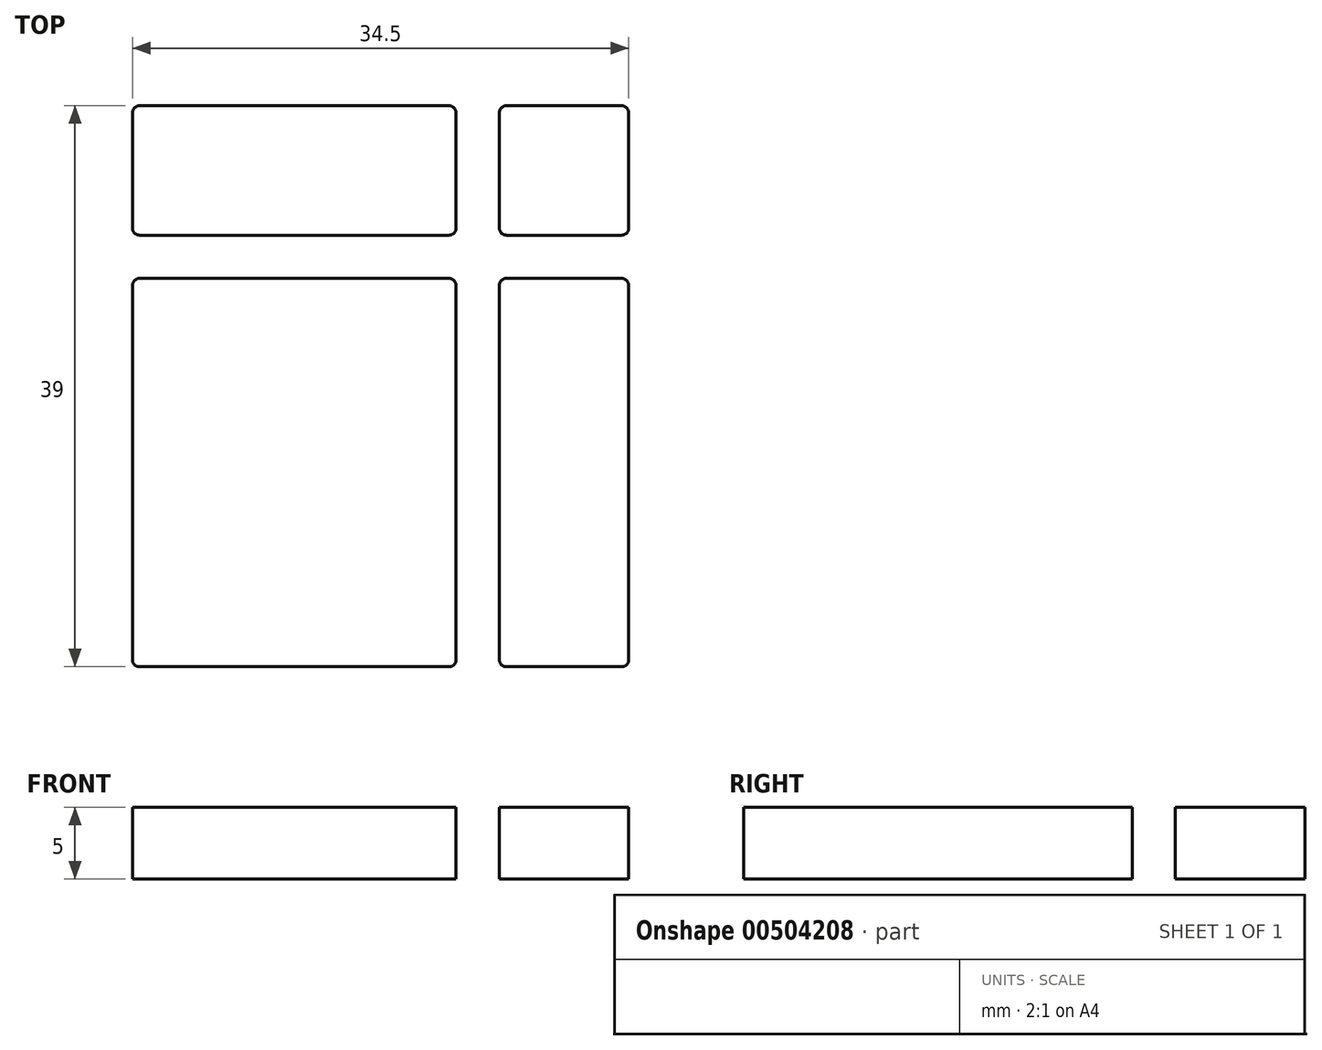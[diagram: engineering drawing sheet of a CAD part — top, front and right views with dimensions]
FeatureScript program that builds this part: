
annotation { "Feature Type Name" : "Feature", "Feature Type Description" : "" }
export const myFeature = defineFeature(function(context is Context, id is Id, definition is map)
    precondition{}
    {
        {
            var Q0;
            Q0=qCreatedBy(makeId("Top.planeOp"),FACE);
            var sketch = newSketch(context, id + "F0", { "sketchPlane" : qUnion([Q0])});
            skLineSegment(sketch, "E0.bottom", {"start": v(0.5, 0) * mm, "end": v(22, 0) * mm});
            skLineSegment(sketch, "E0.top", {"start": v(0.5, 27) * mm, "end": v(22, 27) * mm});
            skLineSegment(sketch, "E0.left", {"start": v(0, 0.5) * mm, "end": v(0, 26.5) * mm});
            skLineSegment(sketch, "E0.right", {"start": v(22.5, 0.5) * mm, "end": v(22.5, 26.5) * mm});
            skLineSegment(sketch, "E1.bottom", {"start": v(26, 0) * mm, "end": v(34, 0) * mm});
            skLineSegment(sketch, "E1.top", {"start": v(26, 27) * mm, "end": v(34, 27) * mm});
            skLineSegment(sketch, "E1.left", {"start": v(25.5, 0.5) * mm, "end": v(25.5, 26.5) * mm});
            skLineSegment(sketch, "E1.right", {"start": v(34.5, 0.5) * mm, "end": v(34.5, 26.5) * mm});
            skLineSegment(sketch, "E2.bottom", {"start": v(0.5, 30) * mm, "end": v(22, 30) * mm});
            skLineSegment(sketch, "E2.top", {"start": v(0.5, 39) * mm, "end": v(22, 39) * mm});
            skLineSegment(sketch, "E2.left", {"start": v(0, 30.5) * mm, "end": v(0, 38.5) * mm});
            skLineSegment(sketch, "E2.right", {"start": v(22.5, 30.5) * mm, "end": v(22.5, 38.5) * mm});
            skLineSegment(sketch, "E3.bottom", {"start": v(26, 30) * mm, "end": v(34, 30) * mm});
            skLineSegment(sketch, "E3.top", {"start": v(26, 39) * mm, "end": v(34, 39) * mm});
            skLineSegment(sketch, "E3.left", {"start": v(25.5, 30.5) * mm, "end": v(25.5, 38.5) * mm});
            skLineSegment(sketch, "E3.right", {"start": v(34.5, 30.5) * mm, "end": v(34.5, 38.5) * mm});
            skPoint(sketch, "E4.visualSharp", {"position": v(0, 39) * mm});
            skArc(sketch, "E4.filletArc", {"start": v(0.5, 39) * mm, "mid": v(0.15, 38.85) * mm, "end": v(0, 38.5) * mm});
            skPoint(sketch, "E5.visualSharp", {"position": v(22.5, 39) * mm});
            skArc(sketch, "E5.filletArc", {"start": v(22.5, 38.5) * mm, "mid": v(22.35, 38.85) * mm, "end": v(22, 39) * mm});
            skPoint(sketch, "E6.visualSharp", {"position": v(0, 30) * mm});
            skArc(sketch, "E6.filletArc", {"start": v(0, 30.5) * mm, "mid": v(0.15, 30.15) * mm, "end": v(0.5, 30) * mm});
            skPoint(sketch, "E7.visualSharp", {"position": v(22.5, 30) * mm});
            skArc(sketch, "E7.filletArc", {"start": v(22, 30) * mm, "mid": v(22.35, 30.15) * mm, "end": v(22.5, 30.5) * mm});
            skPoint(sketch, "E8.visualSharp", {"position": v(25.5, 30) * mm});
            skArc(sketch, "E8.filletArc", {"start": v(25.5, 30.5) * mm, "mid": v(25.65, 30.15) * mm, "end": v(26, 30) * mm});
            skPoint(sketch, "E9.visualSharp", {"position": v(34.5, 30) * mm});
            skArc(sketch, "E9.filletArc", {"start": v(34, 30) * mm, "mid": v(34.35, 30.15) * mm, "end": v(34.5, 30.5) * mm});
            skPoint(sketch, "E10.visualSharp", {"position": v(34.5, 39) * mm});
            skArc(sketch, "E10.filletArc", {"start": v(34.5, 38.5) * mm, "mid": v(34.35, 38.85) * mm, "end": v(34, 39) * mm});
            skPoint(sketch, "E11.visualSharp", {"position": v(25.5, 39) * mm});
            skArc(sketch, "E11.filletArc", {"start": v(26, 39) * mm, "mid": v(25.65, 38.85) * mm, "end": v(25.5, 38.5) * mm});
            skPoint(sketch, "E12.visualSharp", {"position": v(25.5, 27) * mm});
            skArc(sketch, "E12.filletArc", {"start": v(26, 27) * mm, "mid": v(25.65, 26.85) * mm, "end": v(25.5, 26.5) * mm});
            skPoint(sketch, "E13.visualSharp", {"position": v(34.5, 27) * mm});
            skArc(sketch, "E13.filletArc", {"start": v(34.5, 26.5) * mm, "mid": v(34.35, 26.85) * mm, "end": v(34, 27) * mm});
            skPoint(sketch, "E14.visualSharp", {"position": v(34.5, 0) * mm});
            skArc(sketch, "E14.filletArc", {"start": v(34, 0) * mm, "mid": v(34.35, 0.15) * mm, "end": v(34.5, 0.5) * mm});
            skPoint(sketch, "E15.visualSharp", {"position": v(25.5, 0) * mm});
            skArc(sketch, "E15.filletArc", {"start": v(25.5, 0.5) * mm, "mid": v(25.65, 0.15) * mm, "end": v(26, 0) * mm});
            skPoint(sketch, "E16.visualSharp", {"position": v(22.5, 0) * mm});
            skArc(sketch, "E16.filletArc", {"start": v(22, 0) * mm, "mid": v(22.35, 0.15) * mm, "end": v(22.5, 0.5) * mm});
            skPoint(sketch, "E17.visualSharp", {"position": v(22.5, 27) * mm});
            skArc(sketch, "E17.filletArc", {"start": v(22.5, 26.5) * mm, "mid": v(22.35, 26.85) * mm, "end": v(22, 27) * mm});
            skPoint(sketch, "E18.visualSharp", {"position": v(0, 27) * mm});
            skArc(sketch, "E18.filletArc", {"start": v(0.5, 27) * mm, "mid": v(0.15, 26.85) * mm, "end": v(0, 26.5) * mm});
            skPoint(sketch, "E19.visualSharp", {"position": v(0, 0) * mm});
            skArc(sketch, "E19.filletArc", {"start": v(0, 0.5) * mm, "mid": v(0.15, 0.15) * mm, "end": v(0.5, 0) * mm});
            skSolve(sketch);
        }
        {
            var Q0;
            Q0 = qSketchRegion(id + "F0", true);
            extrude(context, id + "F1", {"entities" : qUnion([Q0]), "depth" : 5 * mm});
        }
    });
